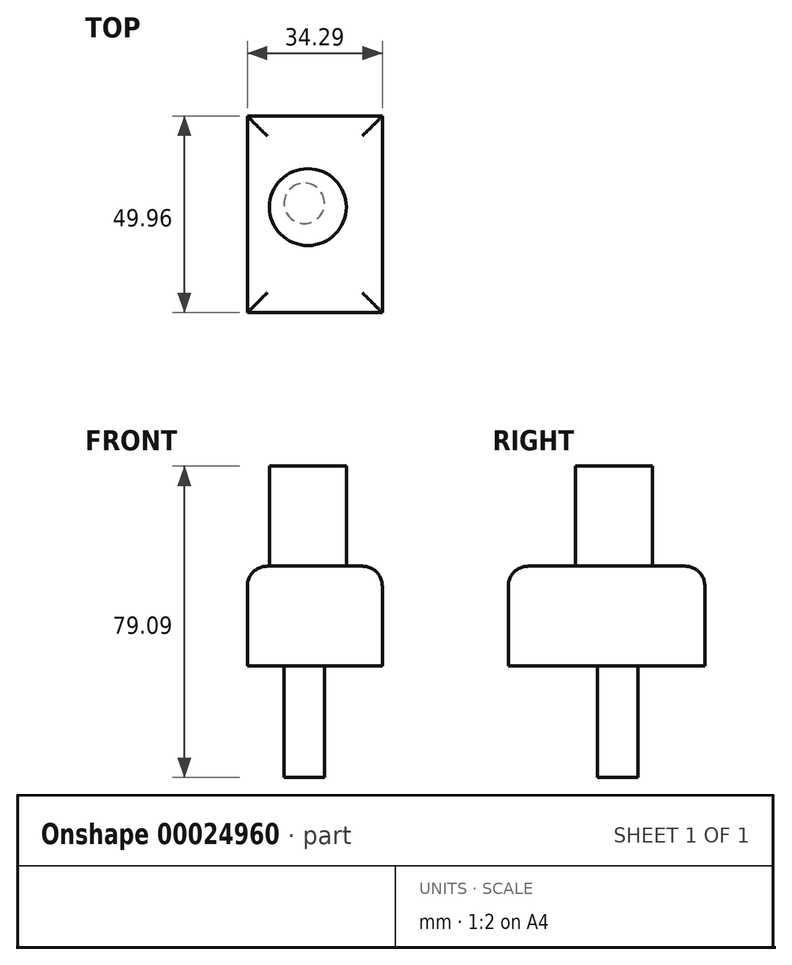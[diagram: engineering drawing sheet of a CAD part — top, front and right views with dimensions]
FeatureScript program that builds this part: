
annotation { "Feature Type Name" : "Feature", "Feature Type Description" : "" }
export const myFeature = defineFeature(function(context is Context, id is Id, definition is map)
    precondition{}
    {
        {
            var Q0;
            Q0=qCreatedBy(makeId("Top.planeOp"),FACE);
            var sketch = newSketch(context, id + "F0", { "sketchPlane" : qUnion([Q0])});
            skLineSegment(sketch, "E0.bottom", {"start": v(0, 0) * mm, "end": v(34.3, 0) * mm});
            skLineSegment(sketch, "E0.top", {"start": v(0, 49.96) * mm, "end": v(34.3, 49.96) * mm});
            skLineSegment(sketch, "E0.left", {"start": v(0, 0) * mm, "end": v(0, 49.96) * mm});
            skLineSegment(sketch, "E0.right", {"start": v(34.3, 0) * mm, "end": v(34.3, 49.96) * mm});
            skSolve(sketch);
        }
        {
            var Q0;
            Q0=makeQuery(id+"F0.imprint","IMPRINT",FACE,{"disambiguationData":[TD([[makeQuery(id+"F0.imprint","IMPRINT",EDGE,{"derivedFrom":sQuery(id+"F0.wireOp",EDGE,"E0.bottom")}),1.0]])]});
            extrude(context, id + "F1", {"entities" : qUnion([Q0]), "depth" : 25.4 * mm});
        }
        {
            var Q0;
            Q0=makeQuery(id+"F1.opExtrude","CAP_FACE",FACE,{"disambiguationData":[OSD([sQuery(id+"F0.wireOp",EDGE,"E0.bottom"),sQuery(id+"F0.wireOp",EDGE,"E0.top"),sQuery(id+"F0.wireOp",EDGE,"E0.left"),sQuery(id+"F0.wireOp",EDGE,"E0.right")])],"isStart":false});
            var sketch = newSketch(context, id + "F2", { "sketchPlane" : qUnion([Q0])});
            skCircle(sketch, "E1", {"center": v(15.38, 26.83) * mm, "radius": 9.76 * mm});
            skSolve(sketch);
        }
        {
            var Q0;
            Q0 = qSketchRegion(id + "F2", true);
            extrude(context, id + "F3", {"entities" : qUnion([Q0]), "operationType" : NewBodyOperationType.ADD, "depth" : 25.4 * mm});
        }
        {
            var Q0;
            Q0=makeQuery(id+"F3.opExtrude","CAP_FACE",FACE,{"disambiguationData":[OSD([sQuery(id+"F2.wireOp",EDGE,"E1")])],"isStart":false});
            var sketch = newSketch(context, id + "F4", { "sketchPlane" : qUnion([Q0])});
            skSolve(sketch);
        }
        {
            var Q0;
            Q0=makeQuery(id+"F4.imprint","IMPRINT",FACE,{"disambiguationData":[TD([[makeQuery(id+"F4.imprint","IMPRINT",EDGE,{"derivedFrom":makeQuery(id+"F3.opExtrude","CAP_EDGE",EDGE,{"disambiguationData":[OSD([sQuery(id+"F2.wireOp",EDGE,"E1")])],"isStart":false})}),1.0]])]});
            var sketch = newSketch(context, id + "F5", { "sketchPlane" : qUnion([Q0])});
            skCircle(sketch, "E2", {"center": v(14.5, 27.76) * mm, "radius": 5.13 * mm});
            skSolve(sketch);
        }
        {
            var Q0;
            Q0 = qSketchRegion(id + "F5", true);
            extrude(context, id + "F6", {"entities" : qUnion([Q0]), "operationType" : NewBodyOperationType.ADD, "endBound" : BoundingType.THROUGH_ALL, "oppositeDirection" : true, "depth" : 25.4 * mm});
        }
        {
            var Q0;
            Q0=makeQuery(id+"F1.opExtrude","CAP_EDGE",EDGE,{"disambiguationData":[OSD([sQuery(id+"F0.wireOp",EDGE,"E0.bottom")])],"isStart":false});
            var Q1;
            Q1=makeQuery(id+"F1.opExtrude","CAP_EDGE",EDGE,{"disambiguationData":[OSD([sQuery(id+"F0.wireOp",EDGE,"E0.right")])],"isStart":false});
            var Q2;
            Q2=makeQuery(id+"F1.opExtrude","CAP_EDGE",EDGE,{"disambiguationData":[OSD([sQuery(id+"F0.wireOp",EDGE,"E0.left")])],"isStart":false});
            var Q3;
            Q3=makeQuery(id+"F1.opExtrude","CAP_EDGE",EDGE,{"disambiguationData":[OSD([sQuery(id+"F0.wireOp",EDGE,"E0.top")])],"isStart":false});
            fillet(context, id + "F7", {"entities" : qUnion([Q0, Q1, Q2, Q3]), "radius" : 5.08 * mm, "tangentPropagation" : true, "allowEdgeOverflow" : false});
        }
        {
            var Q0;
            Q0=makeQuery(id+"F1.opExtrude","SWEPT_FACE",FACE,{"disambiguationData":[OSD([sQuery(id+"F0.wireOp",EDGE,"E0.bottom")])]});
            var sketch = newSketch(context, id + "F8", { "sketchPlane" : qUnion([Q0])});
            skCircle(sketch, "E3", {"center": v(8.85, 13.27) * mm, "radius": 4.44 * mm});
            skSolve(sketch);
        }
        {
            var Q0;
            Q0=sQuery(id+"F8.wireOp",EDGE,"E3");
            extrude(context, id + "F9", {"bodyType" : ToolBodyType.SURFACE, "surfaceEntities" : qUnion([Q0]), "depth" : 25.4 * mm});
        }
    });
